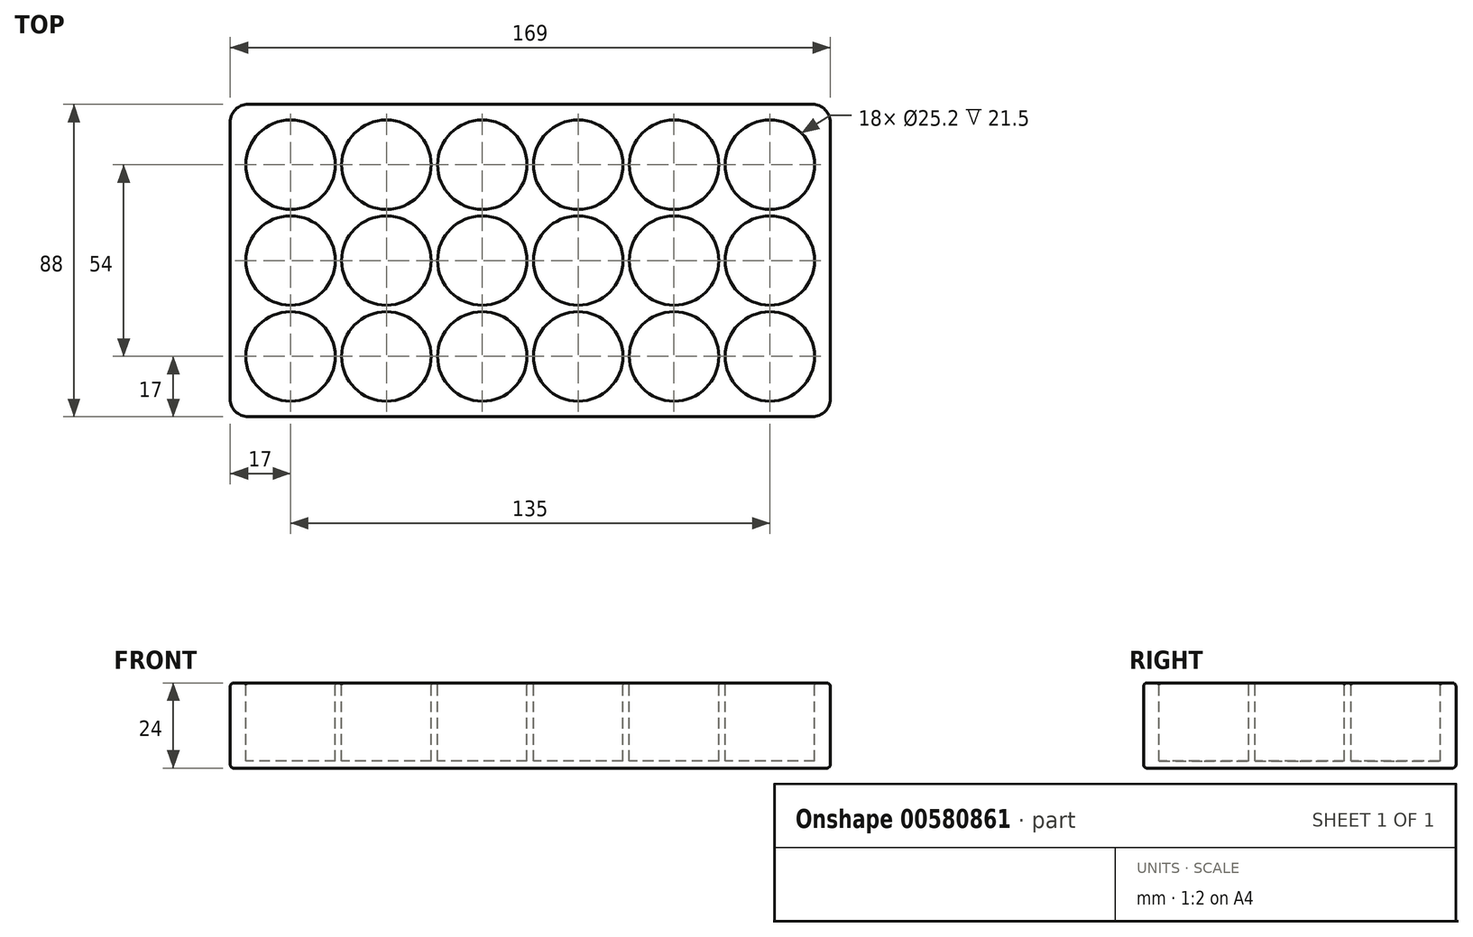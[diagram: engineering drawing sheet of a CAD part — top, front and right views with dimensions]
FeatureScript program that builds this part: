
annotation { "Feature Type Name" : "Feature", "Feature Type Description" : "" }
export const myFeature = defineFeature(function(context is Context, id is Id, definition is map)
    precondition{}
    {
        {
            var Q0;
            Q0=qCreatedBy(makeId("Top.planeOp"),FACE);
            var sketch = newSketch(context, id + "F0", { "sketchPlane" : qUnion([Q0])});
            skPoint(sketch, "E0.middle", {"position": v(0, 0) * mm});
            skCircle(sketch, "E1", {"center": v(0, 0) * mm, "radius": 12.6 * mm});
            skCircle(sketch, "E2.0.1.0", {"center": v(0, 27) * mm, "radius": 12.6 * mm});
            skCircle(sketch, "E2.0.2.0", {"center": v(0, 54) * mm, "radius": 12.6 * mm});
            skCircle(sketch, "E2.1.0.0", {"center": v(27, 0) * mm, "radius": 12.6 * mm});
            skCircle(sketch, "E2.1.1.0", {"center": v(27, 27) * mm, "radius": 12.6 * mm});
            skCircle(sketch, "E2.1.2.0", {"center": v(27, 54) * mm, "radius": 12.6 * mm});
            skCircle(sketch, "E2.2.0.0", {"center": v(54, 0) * mm, "radius": 12.6 * mm});
            skCircle(sketch, "E2.2.1.0", {"center": v(54, 27) * mm, "radius": 12.6 * mm});
            skCircle(sketch, "E2.2.2.0", {"center": v(54, 54) * mm, "radius": 12.6 * mm});
            skCircle(sketch, "E2.3.0.0", {"center": v(81, 0) * mm, "radius": 12.6 * mm});
            skCircle(sketch, "E2.3.1.0", {"center": v(81, 27) * mm, "radius": 12.6 * mm});
            skCircle(sketch, "E2.3.2.0", {"center": v(81, 54) * mm, "radius": 12.6 * mm});
            skCircle(sketch, "E2.4.0.0", {"center": v(108, 0) * mm, "radius": 12.6 * mm});
            skCircle(sketch, "E2.4.1.0", {"center": v(108, 27) * mm, "radius": 12.6 * mm});
            skCircle(sketch, "E2.4.2.0", {"center": v(108, 54) * mm, "radius": 12.6 * mm});
            skCircle(sketch, "E2.5.0.0", {"center": v(135, 0) * mm, "radius": 12.6 * mm});
            skCircle(sketch, "E2.5.1.0", {"center": v(135, 27) * mm, "radius": 12.6 * mm});
            skCircle(sketch, "E2.5.2.0", {"center": v(135, 54) * mm, "radius": 12.6 * mm});
            skLineSegment(sketch, "E2.direction1", {"start": v(0, 0) * mm, "end": v(27, 0) * mm, "construction": true});
            skLineSegment(sketch, "E2.direction2", {"start": v(0, 0) * mm, "end": v(0, 27) * mm, "construction": true});
            skLineSegment(sketch, "E3.bottom", {"start": v(-17, 71) * mm, "end": v(152, 71) * mm});
            skLineSegment(sketch, "E3.top", {"start": v(-17, -17) * mm, "end": v(152, -17) * mm});
            skLineSegment(sketch, "E3.left", {"start": v(-17, 71) * mm, "end": v(-17, -17) * mm});
            skLineSegment(sketch, "E3.right", {"start": v(152, 71) * mm, "end": v(152, -17) * mm});
            skSolve(sketch);
        }
        {
            var Q0;
            Q0 = qSketchRegion(id + "F0", true);
            extrude(context, id + "F1", {"entities" : qUnion([Q0]), "oppositeDirection" : true, "depth" : 22 * mm, "offsetDistance" : 25 * mm});
        }
        {
            var Q0;
            Q0=makeQuery(id+"F1.opExtrude","CAP_FACE",FACE,{"disambiguationData":[OSD([sQuery(id+"F0.wireOp",EDGE,"E1"),sQuery(id+"F0.wireOp",EDGE,"E2.0.1.0"),sQuery(id+"F0.wireOp",EDGE,"E2.0.2.0"),sQuery(id+"F0.wireOp",EDGE,"E2.1.0.0"),sQuery(id+"F0.wireOp",EDGE,"E2.1.1.0"),sQuery(id+"F0.wireOp",EDGE,"E2.1.2.0"),sQuery(id+"F0.wireOp",EDGE,"E2.2.0.0"),sQuery(id+"F0.wireOp",EDGE,"E2.2.1.0"),sQuery(id+"F0.wireOp",EDGE,"E2.2.2.0"),sQuery(id+"F0.wireOp",EDGE,"E2.3.0.0"),sQuery(id+"F0.wireOp",EDGE,"E2.3.1.0"),sQuery(id+"F0.wireOp",EDGE,"E2.3.2.0"),sQuery(id+"F0.wireOp",EDGE,"E2.4.0.0"),sQuery(id+"F0.wireOp",EDGE,"E2.4.1.0"),sQuery(id+"F0.wireOp",EDGE,"E2.4.2.0"),sQuery(id+"F0.wireOp",EDGE,"E2.5.0.0"),sQuery(id+"F0.wireOp",EDGE,"E2.5.1.0"),sQuery(id+"F0.wireOp",EDGE,"E2.5.2.0"),sQuery(id+"F0.wireOp",EDGE,"E3.bottom"),sQuery(id+"F0.wireOp",EDGE,"E3.top"),sQuery(id+"F0.wireOp",EDGE,"E3.left"),sQuery(id+"F0.wireOp",EDGE,"E3.right")])],"isStart":false});
            var sketch = newSketch(context, id + "F2", { "sketchPlane" : qUnion([Q0])});
            skLineSegment(sketch, "E4.bottom", {"start": v(152, -71) * mm, "end": v(-17, -71) * mm});
            skLineSegment(sketch, "E4.top", {"start": v(152, 17) * mm, "end": v(-17, 17) * mm});
            skLineSegment(sketch, "E4.left", {"start": v(152, -71) * mm, "end": v(152, 17) * mm});
            skLineSegment(sketch, "E4.right", {"start": v(-17, -71) * mm, "end": v(-17, 17) * mm});
            skSolve(sketch);
        }
        {
            var Q0;
            Q0 = qSketchRegion(id + "F2", true);
            extrude(context, id + "F3", {"entities" : qUnion([Q0]), "operationType" : NewBodyOperationType.ADD, "depth" : 2 * mm, "offsetDistance" : 25 * mm});
        }
        {
            var Q0;
            Q0=makeQuery(id+"F1.opExtrude","CAP_EDGE",EDGE,{"disambiguationData":[OSD([sQuery(id+"F0.wireOp",EDGE,"E3.left")])],"isStart":true});
            var Q1;
            Q1=makeQuery(id+"F1.opExtrude","CAP_EDGE",EDGE,{"disambiguationData":[OSD([sQuery(id+"F0.wireOp",EDGE,"E3.bottom")])],"isStart":true});
            var Q2;
            Q2=makeQuery(id+"F1.opExtrude","CAP_EDGE",EDGE,{"disambiguationData":[OSD([sQuery(id+"F0.wireOp",EDGE,"E3.right")])],"isStart":true});
            var Q3;
            Q3=makeQuery(id+"F1.opExtrude","CAP_EDGE",EDGE,{"disambiguationData":[OSD([sQuery(id+"F0.wireOp",EDGE,"E3.top")])],"isStart":true});
            var Q4;
            Q4=makeQuery(id+"F3.opExtrude","CAP_FACE",FACE,{"disambiguationData":[OSD([sQuery(id+"F2.wireOp",EDGE,"E4.bottom"),sQuery(id+"F2.wireOp",EDGE,"E4.top"),sQuery(id+"F2.wireOp",EDGE,"E4.left"),sQuery(id+"F2.wireOp",EDGE,"E4.right")])],"isStart":false});
            fillet(context, id + "F4", {"entities" : qUnion([Q0, Q1, Q2, Q3, Q4]), "radius" : 1 * mm, "tangentPropagation" : true, "allowEdgeOverflow" : false});
        }
        {
            var Q0;
            Q0=makeQuery(id+"F1.opExtrude","CAP_EDGE",EDGE,{"disambiguationData":[OSD([sQuery(id+"F0.wireOp",EDGE,"E2.5.0.0")])],"isStart":true});
            var Q1;
            Q1=makeQuery(id+"F1.opExtrude","CAP_FACE",FACE,{"disambiguationData":[OSD([sQuery(id+"F0.wireOp",EDGE,"E1"),sQuery(id+"F0.wireOp",EDGE,"E2.0.1.0"),sQuery(id+"F0.wireOp",EDGE,"E2.0.2.0"),sQuery(id+"F0.wireOp",EDGE,"E2.1.0.0"),sQuery(id+"F0.wireOp",EDGE,"E2.1.1.0"),sQuery(id+"F0.wireOp",EDGE,"E2.1.2.0"),sQuery(id+"F0.wireOp",EDGE,"E2.2.0.0"),sQuery(id+"F0.wireOp",EDGE,"E2.2.1.0"),sQuery(id+"F0.wireOp",EDGE,"E2.2.2.0"),sQuery(id+"F0.wireOp",EDGE,"E2.3.0.0"),sQuery(id+"F0.wireOp",EDGE,"E2.3.1.0"),sQuery(id+"F0.wireOp",EDGE,"E2.3.2.0"),sQuery(id+"F0.wireOp",EDGE,"E2.4.0.0"),sQuery(id+"F0.wireOp",EDGE,"E2.4.1.0"),sQuery(id+"F0.wireOp",EDGE,"E2.4.2.0"),sQuery(id+"F0.wireOp",EDGE,"E2.5.0.0"),sQuery(id+"F0.wireOp",EDGE,"E2.5.1.0"),sQuery(id+"F0.wireOp",EDGE,"E2.5.2.0"),sQuery(id+"F0.wireOp",EDGE,"E3.bottom"),sQuery(id+"F0.wireOp",EDGE,"E3.top"),sQuery(id+"F0.wireOp",EDGE,"E3.left"),sQuery(id+"F0.wireOp",EDGE,"E3.right")])],"isStart":true});
            fillet(context, id + "F5", {"entities" : qUnion([Q0, Q1]), "radius" : .5 * mm, "tangentPropagation" : true, "allowEdgeOverflow" : false});
        }
        {
            var Q0;
            Q0=makeQuery(id+"F3.boolean.opBoolean","MERGE",EDGE,{"derivedFrom":[makeQuery(id+"F1.opExtrude","SWEPT_EDGE",EDGE,{"disambiguationData":[OSD([sQuery(id+"F0.wireOp",EDGE,"E3.bottom"),sQuery(id+"F0.wireOp",EDGE,"E3.left")])]}),makeQuery(id+"F3.opExtrude","SWEPT_EDGE",EDGE,{"disambiguationData":[OSD([sQuery(id+"F2.wireOp",EDGE,"E4.bottom"),sQuery(id+"F2.wireOp",EDGE,"E4.right")])]})]});
            var Q1;
            Q1=makeQuery(id+"F3.boolean.opBoolean","MERGE",EDGE,{"derivedFrom":[makeQuery(id+"F1.opExtrude","SWEPT_EDGE",EDGE,{"disambiguationData":[OSD([sQuery(id+"F0.wireOp",EDGE,"E3.top"),sQuery(id+"F0.wireOp",EDGE,"E3.left")])]}),makeQuery(id+"F3.opExtrude","SWEPT_EDGE",EDGE,{"disambiguationData":[OSD([sQuery(id+"F2.wireOp",EDGE,"E4.top"),sQuery(id+"F2.wireOp",EDGE,"E4.right")])]})]});
            var Q2;
            Q2=makeQuery(id+"F3.boolean.opBoolean","MERGE",EDGE,{"derivedFrom":[makeQuery(id+"F1.opExtrude","SWEPT_EDGE",EDGE,{"disambiguationData":[OSD([sQuery(id+"F0.wireOp",EDGE,"E3.bottom"),sQuery(id+"F0.wireOp",EDGE,"E3.right")])]}),makeQuery(id+"F3.opExtrude","SWEPT_EDGE",EDGE,{"disambiguationData":[OSD([sQuery(id+"F2.wireOp",EDGE,"E4.bottom"),sQuery(id+"F2.wireOp",EDGE,"E4.left")])]})]});
            var Q3;
            Q3=makeQuery(id+"F3.boolean.opBoolean","MERGE",EDGE,{"derivedFrom":[makeQuery(id+"F1.opExtrude","SWEPT_EDGE",EDGE,{"disambiguationData":[OSD([sQuery(id+"F0.wireOp",EDGE,"E3.top"),sQuery(id+"F0.wireOp",EDGE,"E3.right")])]}),makeQuery(id+"F3.opExtrude","SWEPT_EDGE",EDGE,{"disambiguationData":[OSD([sQuery(id+"F2.wireOp",EDGE,"E4.top"),sQuery(id+"F2.wireOp",EDGE,"E4.left")])]})]});
            fillet(context, id + "F6", {"entities" : qUnion([Q0, Q1, Q2, Q3]), "radius" : 5 * mm, "tangentPropagation" : true, "allowEdgeOverflow" : false});
        }
    });
